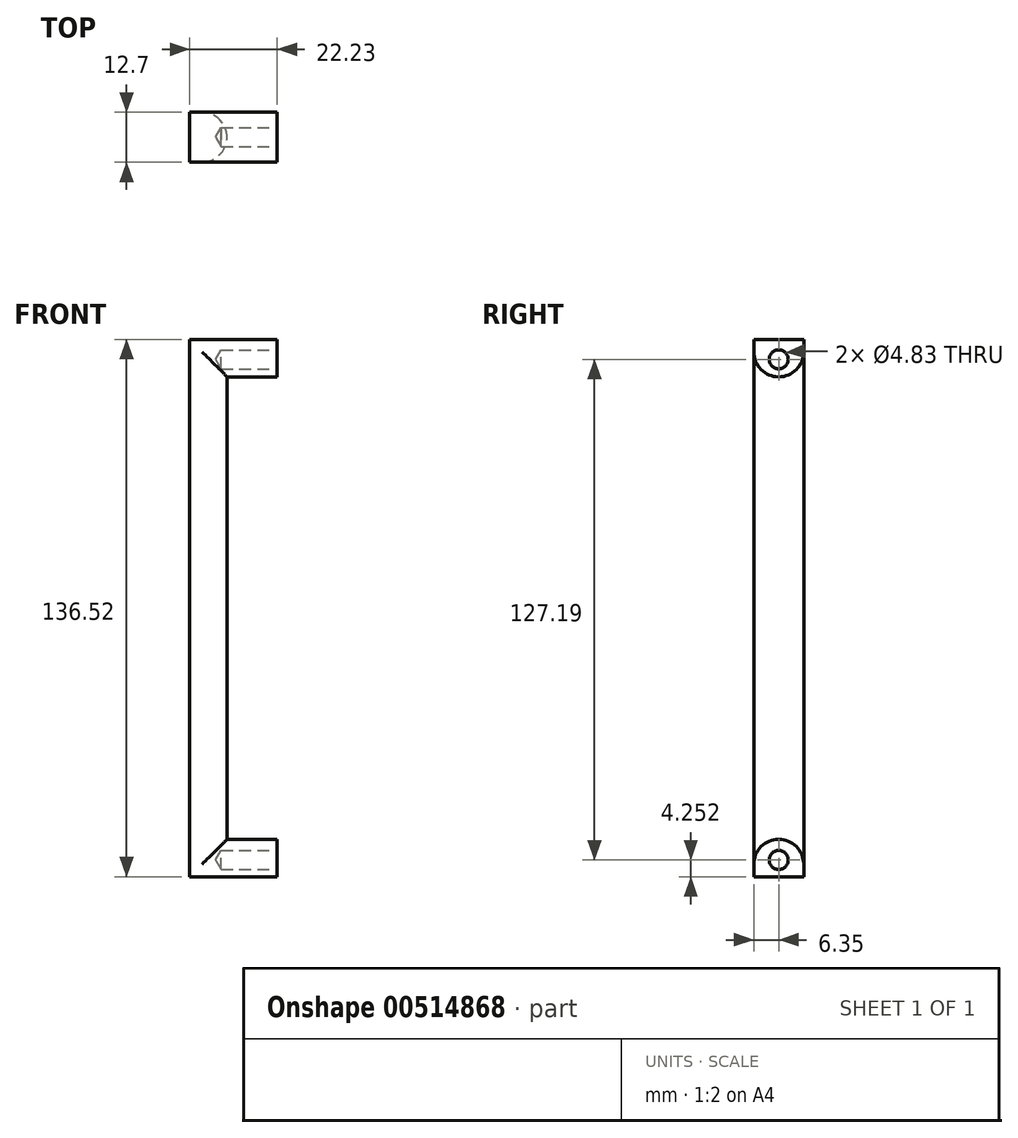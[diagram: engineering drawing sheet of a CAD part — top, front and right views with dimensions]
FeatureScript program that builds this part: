
annotation { "Feature Type Name" : "Feature", "Feature Type Description" : "" }
export const myFeature = defineFeature(function(context is Context, id is Id, definition is map)
    precondition{}
    {
        {
            var Q0;
            Q0=qCreatedBy(makeId("Front.planeOp"),FACE);
            var sketch = newSketch(context, id + "F0", { "sketchPlane" : qUnion([Q0])});
            skLineSegment(sketch, "E0.bottom", {"start": v(12.7, 68.26) * mm, "end": v(-12.7, 68.26) * mm});
            skLineSegment(sketch, "E0.top", {"start": v(12.7, -68.26) * mm, "end": v(-12.7, -68.26) * mm});
            skLineSegment(sketch, "E0.left", {"start": v(12.7, 68.26) * mm, "end": v(12.7, -68.26) * mm});
            skLineSegment(sketch, "E0.right", {"start": v(-12.7, 68.26) * mm, "end": v(-12.7, -68.26) * mm});
            skPoint(sketch, "E0.middle", {"position": v(0, 0) * mm});
            skLineSegment(sketch, "E1.bottom", {"start": v(12.7, 64) * mm, "end": v(12.7, 64) * mm});
            skLineSegment(sketch, "E1.top", {"start": v(12.7, -64) * mm, "end": v(12.7, -64) * mm});
            skLineSegment(sketch, "E1.left", {"start": v(12.7, 64) * mm, "end": v(12.7, -64) * mm});
            skLineSegment(sketch, "E1.right", {"start": v(12.7, 64) * mm, "end": v(12.7, -64) * mm});
            skPoint(sketch, "E1.middle", {"position": v(12.7, 0) * mm});
            skLineSegment(sketch, "E2", {"start": v(12.7, -68.26) * mm, "end": v(12.7, -58.74) * mm});
            skLineSegment(sketch, "E3", {"start": v(12.7, 68.26) * mm, "end": v(12.7, 58.74) * mm});
            skLineSegment(sketch, "E4", {"start": v(12.7, 58.74) * mm, "end": v(0, 58.74) * mm});
            skLineSegment(sketch, "E5", {"start": v(0, 58.74) * mm, "end": v(0, -58.74) * mm});
            skLineSegment(sketch, "E6", {"start": v(0, -58.74) * mm, "end": v(12.7, -58.74) * mm});
            skSolve(sketch);
        }
        {
            var Q0;
            {var subQ1=sQuery(id+"F0.wireOp",EDGE,"E0.bottom");Q0=makeQuery(id+"F0.imprint","IMPRINT",FACE,{"disambiguationData":[TD([[makeQuery(id+"F0.imprint","IMPRINT",EDGE,{"derivedFrom":subQ1}),1.0]])]});}
            extrude(context, id + "F1", {"entities" : qUnion([Q0]), "depth" : 12.7 * mm, "offsetDistance" : 25.4 * mm});
        }
        {
            var Q0;
            Q0=makeQuery(id+"F1.opExtrude","CAP_EDGE",EDGE,{"disambiguationData":[OSD([sQuery(id+"F0.wireOp",EDGE,"E5")])],"isStart":false});
            var Q1;
            Q1=makeQuery(id+"F1.opExtrude","CAP_EDGE",EDGE,{"disambiguationData":[OSD([sQuery(id+"F0.wireOp",EDGE,"E5")])],"isStart":true});
            fillet(context, id + "F2", {"entities" : qUnion([Q0, Q1]), "tangentPropagation" : true, "radius" : 6.35 * mm, "defaultsChanged" : true, "vertexSettings" : [], "allowEdgeOverflow" : false});
        }
        {
            var Q0;
            Q0=makeQuery(id+"F1.opExtrude","CAP_EDGE",EDGE,{"disambiguationData":[OSD([sQuery(id+"F0.wireOp",EDGE,"E4")])],"isStart":false});
            var Q1;
            Q1=makeQuery(id+"F1.opExtrude","CAP_EDGE",EDGE,{"disambiguationData":[OSD([sQuery(id+"F0.wireOp",EDGE,"E4")])],"isStart":true});
            var Q2;
            Q2=makeQuery(id+"F1.opExtrude","CAP_EDGE",EDGE,{"disambiguationData":[OSD([sQuery(id+"F0.wireOp",EDGE,"E6")])],"isStart":false});
            var Q3;
            Q3=makeQuery(id+"F1.opExtrude","CAP_EDGE",EDGE,{"disambiguationData":[OSD([sQuery(id+"F0.wireOp",EDGE,"E6")])],"isStart":true});
            fillet(context, id + "F3", {"entities" : qUnion([Q0, Q1, Q2, Q3]), "tangentPropagation" : true, "radius" : 6.35 * mm, "defaultsChanged" : true, "vertexSettings" : [], "allowEdgeOverflow" : false});
        }
        {
            var Q0;
            Q0=makeQuery(id+"F1.opExtrude","SWEPT_FACE",FACE,{"disambiguationData":[OSD([sQuery(id+"F0.wireOp",EDGE,"E0.right")])]});
            extrude(context, id + "F4", {"entities" : qUnion([Q0]), "operationType" : NewBodyOperationType.REMOVE, "oppositeDirection" : true, "depth" : 3.17 * mm, "offsetDistance" : 25.4 * mm});
        }
        {
            var Q0;
            {var subQ0=sQuery(id+"F0.wireOp",EDGE,"E0.left");Q0=makeQuery(id+"F1.opExtrude","SWEPT_FACE",FACE,{"disambiguationData":[OSD([subQ0]),TDD([makeQuery(id+"F0.imprint","IMPRINT",EDGE,{"disambiguationData":[TD([[makeQuery(id+"F0.imprint","INTERSECT",VERTEX,{"derivedFrom":[sQuery(id+"F0.wireOp",EDGE,"E0.bottom"),subQ0]}),-1.0]])],"derivedFrom":subQ0})])]});}
            var sketch = newSketch(context, id + "F5", { "sketchPlane" : qUnion([Q0])});
            skLineSegment(sketch, "E7", {"start": v(-6.35, 68.26) * mm, "end": v(-6.35, 63.18) * mm});
            skPoint(sketch, "E8", {"position": v(-6.35, 63.18) * mm});
            skSolve(sketch);
        }
        {
            var Q0;
            Q0=sQuery(id+"F5.wireOp",VERTEX,"E8");
            var Q1;
            Q1=makeQuery(id+"F1.opExtrude","SWEPT_BODY",BODY,{"disambiguationData":[OSD([sQuery(id+"F0.wireOp",EDGE,"E0.bottom"),sQuery(id+"F0.wireOp",EDGE,"E0.top"),sQuery(id+"F0.wireOp",EDGE,"E0.left"),sQuery(id+"F0.wireOp",EDGE,"E0.right"),sQuery(id+"F0.wireOp",EDGE,"E4"),sQuery(id+"F0.wireOp",EDGE,"E5"),sQuery(id+"F0.wireOp",EDGE,"E6")])]});
            hole(context, id + "F6", {"style" : HoleStyle.SIMPLE, "endStyle" : HoleEndStyle.BLIND, "holeDiameter" : 4.83 * mm, "majorDiameter" : 6.35 * mm, "holeDepth" : 14.22 * mm, "isTappedThrough" : true, "tappedDepth" : 12.7 * mm, "tapClearance" : 3, "startFromSketch" : true, "locations" : qUnion([Q0]), "scope" : qUnion([Q1])});
        }
        {
            var Q0;
            {var subQ0=sQuery(id+"F0.wireOp",EDGE,"E0.left");var subQ1=makeQuery(id+"F0.imprint","IMPRINT",VERTEX,{"derivedFrom":subQ0});Q0=makeQuery(id+"F1.opExtrude","SWEPT_FACE",FACE,{"disambiguationData":[OSD([subQ0]),TDD([makeQuery(id+"F0.imprint","IMPRINT",EDGE,{"disambiguationData":[TD([[subQ1,-1.0]])],"derivedFrom":subQ0}),makeQuery(id+"F0.imprint","IMPRINT",EDGE,{"disambiguationData":[TD([[subQ1,1.0]])],"derivedFrom":subQ0})])]});}
            var sketch = newSketch(context, id + "F7", { "sketchPlane" : qUnion([Q0])});
            skLineSegment(sketch, "E9", {"start": v(-6.35, -69.09) * mm, "end": v(-6.35, -64) * mm});
            skPoint(sketch, "E10", {"position": v(-6.35, -64) * mm});
            skSolve(sketch);
        }
        {
            var Q0;
            Q0=sQuery(id+"F7.wireOp",VERTEX,"E10");
            var Q1;
            Q1=makeQuery(id+"F1.opExtrude","SWEPT_BODY",BODY,{"disambiguationData":[OSD([sQuery(id+"F0.wireOp",EDGE,"E0.bottom"),sQuery(id+"F0.wireOp",EDGE,"E0.top"),sQuery(id+"F0.wireOp",EDGE,"E0.left"),sQuery(id+"F0.wireOp",EDGE,"E0.right"),sQuery(id+"F0.wireOp",EDGE,"E4"),sQuery(id+"F0.wireOp",EDGE,"E5"),sQuery(id+"F0.wireOp",EDGE,"E6")])]});
            hole(context, id + "F8", {"style" : HoleStyle.SIMPLE, "endStyle" : HoleEndStyle.BLIND, "holeDiameter" : 4.83 * mm, "majorDiameter" : 6.35 * mm, "holeDepth" : 14.22 * mm, "isTappedThrough" : true, "tappedDepth" : 12.7 * mm, "tapClearance" : 3, "startFromSketch" : true, "locations" : qUnion([Q0]), "scope" : qUnion([Q1])});
        }
    });
